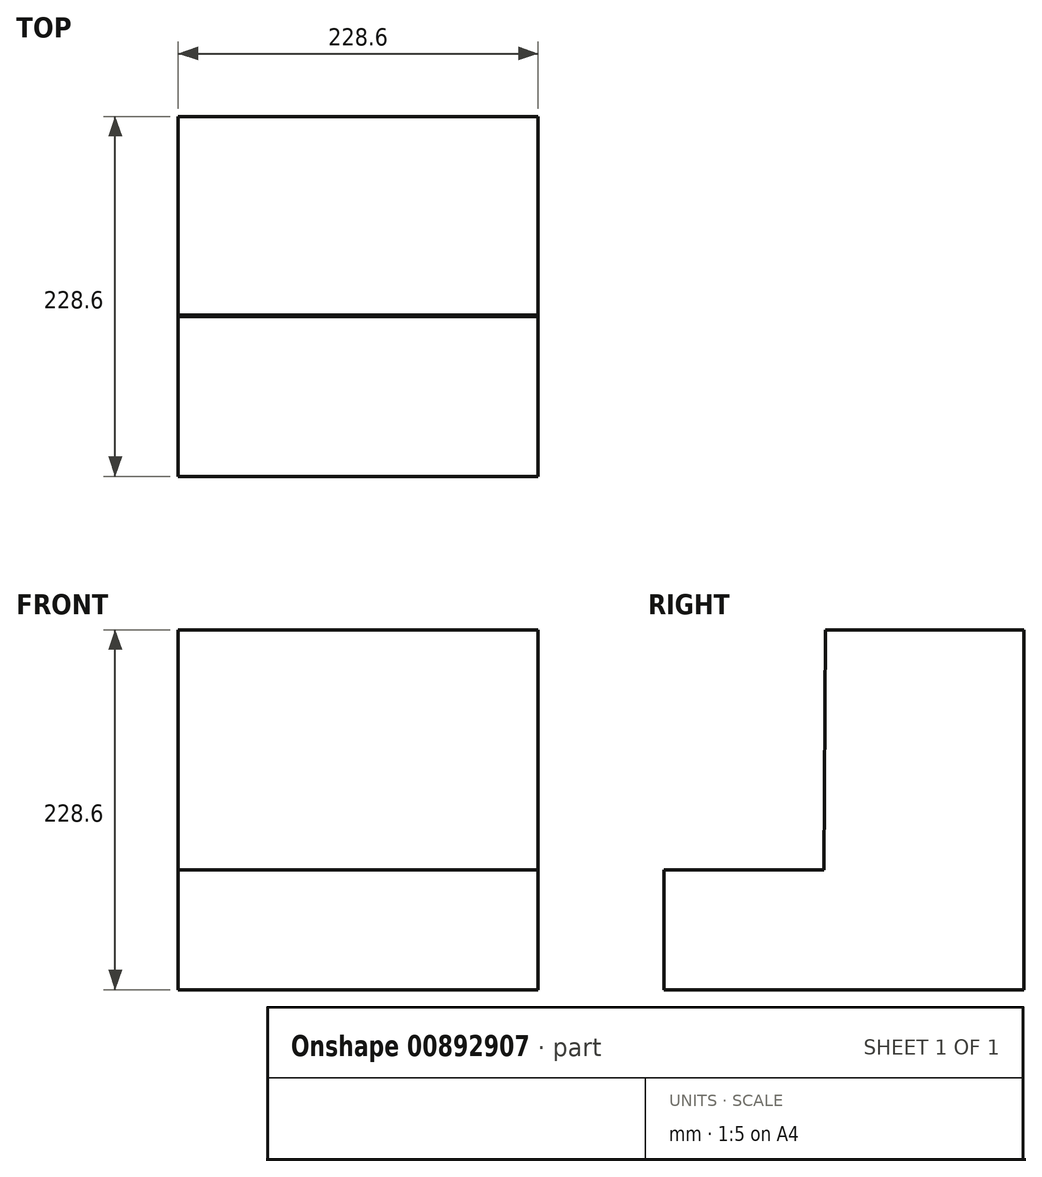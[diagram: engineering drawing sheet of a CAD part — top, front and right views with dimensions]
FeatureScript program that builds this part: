
annotation { "Feature Type Name" : "Feature", "Feature Type Description" : "" }
export const myFeature = defineFeature(function(context is Context, id is Id, definition is map)
    precondition{}
    {
        {
            var Q0;
            Q0=qCreatedBy(makeId("Right.planeOp"),FACE);
            var sketch = newSketch(context, id + "F0", { "sketchPlane" : qUnion([Q0])});
            skLineSegment(sketch, "E0", {"start": v(-34.37, 228.6) * mm, "end": v(91.9, 228.6) * mm});
            skLineSegment(sketch, "E1", {"start": v(91.9, 228.6) * mm, "end": v(91.9, 0) * mm});
            skLineSegment(sketch, "E2", {"start": v(91.9, 0) * mm, "end": v(-136.7, 0) * mm});
            skLineSegment(sketch, "E3", {"start": v(-136.7, 0) * mm, "end": v(-136.7, 76.2) * mm});
            skLineSegment(sketch, "E4", {"start": v(-136.7, 76.2) * mm, "end": v(-35.1, 76.2) * mm});
            skLineSegment(sketch, "E5", {"start": v(-34.37, 228.6) * mm, "end": v(-35.1, 76.2) * mm});
            skSolve(sketch);
        }
        {
            var Q0;
            Q0=makeQuery(id+"F0.imprint","IMPRINT",FACE,{"disambiguationData":[TD([[makeQuery(id+"F0.imprint","IMPRINT",EDGE,{"derivedFrom":sQuery(id+"F0.wireOp",EDGE,"E0")}),-1.0]])]});
            extrude(context, id + "F1", {"entities" : qUnion([Q0]), "endBound" : BoundingType.SYMMETRIC, "depth" : 228.6 * mm, "offsetDistance" : 25 * mm});
        }
    });
